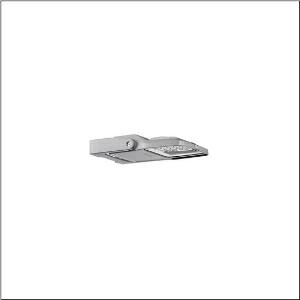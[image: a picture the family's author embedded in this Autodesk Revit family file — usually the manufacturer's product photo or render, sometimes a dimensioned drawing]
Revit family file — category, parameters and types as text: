
# Revit family: floodlight_fl_21_iq_micro___pl61_5xa7762a2c2a_d8df
name_source: partatom
category: Lighting Fixtures
units: mm (PartAtom-declared; Revit-internal decimal feet)

## family parameters
Cut with Voids When Loaded = No
Host = Face
Light Source = No
Part Type = Normal
Room Calculation Point = No
Round Connector Dimension = Use Diameter
Shared = No

## types (1)
- --- (1 x LED, 2910 lm, 23.1 W, 3000K)
    Apparent Load = 23 VA
    CIE Flux Codes = 33 65 98 100 100
    Color Rendering = 70
    Color Temperature = 3000K
    Default Elevation = 1800 mm
    Description = Floodlight FL 21 iQ micro, floodlight, primary light control with lens, of PMMA, primary optical cover: protective disc, of toughened safety glass, transparent, light distribution: PL61, light emission: direct distribution, installation type: surface-mounted, lamps: LED, High Power LED, rated values: 2.910lm | 23,1W | 126lm/W (begin service life); end service life: 2.910lm | 23,8W; at 50% lumin. flux: 1.455lm | 11W | 132,3lm/W, colour temperature: 3000K, colour rendering: CRI > 70, light colour: 730, light setting 1 begin service life: 100% | 2.910lm | 23,1W | 126lm/W | 3.000K, light setting 1 end service life: 23,8W, further light settings possible, control: Auto-Match, Temp-Guard, Night-Set, Smart-Wire, Desk-Remote (wireless, voltage-free reading and setting of iQ features in the workshop via application-optimized NFC function/RFID function), optimised constant luminous flux control (CLO 2.0), Street-Remote, pre-setting: linear dimming characteristic, with terminal, 6-pole, mains connection: 220..240V, AC, 50/60Hz, luminaire housing, of diecast aluminium, powder-coated, SITECO metallic grey (DB 702S), corrosivity category C5 mid according to DIN EN ISO 12944suitable for swimming poolschlorine-resistant, sealing non-destructively replaceable, design bracket, of diecast aluminium, powder-coated, SITECO metallic grey (DB 702S), protection rating (complete): IP66, insulation class (complete): insulation class II (safety insulation), certification: CE, ENEC, VDE, protection symbol: D, impact resistance: IK07, permissible operating ambient temperature: -40..+40°C, permissible operating ambient temperature for outdoor applications: -40..+50°C, standard: DIN EN 12944, LABS conformity tested according to VDMA 24364:2018-05, packaging unit: 1 piece

Light Distribution: PL61
    Height = 65 mm
    Lamp = 1 x LED
    Lamp Light Flux = 2910 lm
    Lamp Power = 23.1 W
    Lamp count = 1
    Length = 312 mm
    Luminous efficacy = 126 lm/W
    Manufacturer = Siteco
    ModVariant = No
    Model = 5XA7762A2C2A
    Mounting Place = Wall
    Mounting Type = Surface mounted
    Number of Poles = 1
    OnlyDefault = Yes
    Power Factor = 1
    Product Name = Floodlight FL 21 iQ micro | PL61
    Product group = floodlight | wall mounted
    ProductGroupID = 2002
    Protection Class = Protection class II
    Protection Degree = IP 66
    RLX_Detail_Level = 1
    RLX_Emergency_Light_Flux = 0 lm
    RLX_Emergency_Type = 0
    RLX_Emergency_Type_DB = No
    RlxData = <blob elided: 97721 chars, md5=daf2ccf9>
    Socket = socket
    Standby Power = 0 W
    System Light Flux = 2910 lm
    System Power = 23 W
    Type Comments = factory setting: luminous flux: 100 % | dim-lin: 254 | 455 mA
    Type Image = l_1006878.jpg
    URL = http://relux.com
    VarID = @adj_193425
    Voltage = 0 V
    Weight = 0.00 kg
    Width = 230 mm

## geometry (parser evidence)
native form markers: Blend x4, Sweep x13
no freeform markers — native parametric forms only
